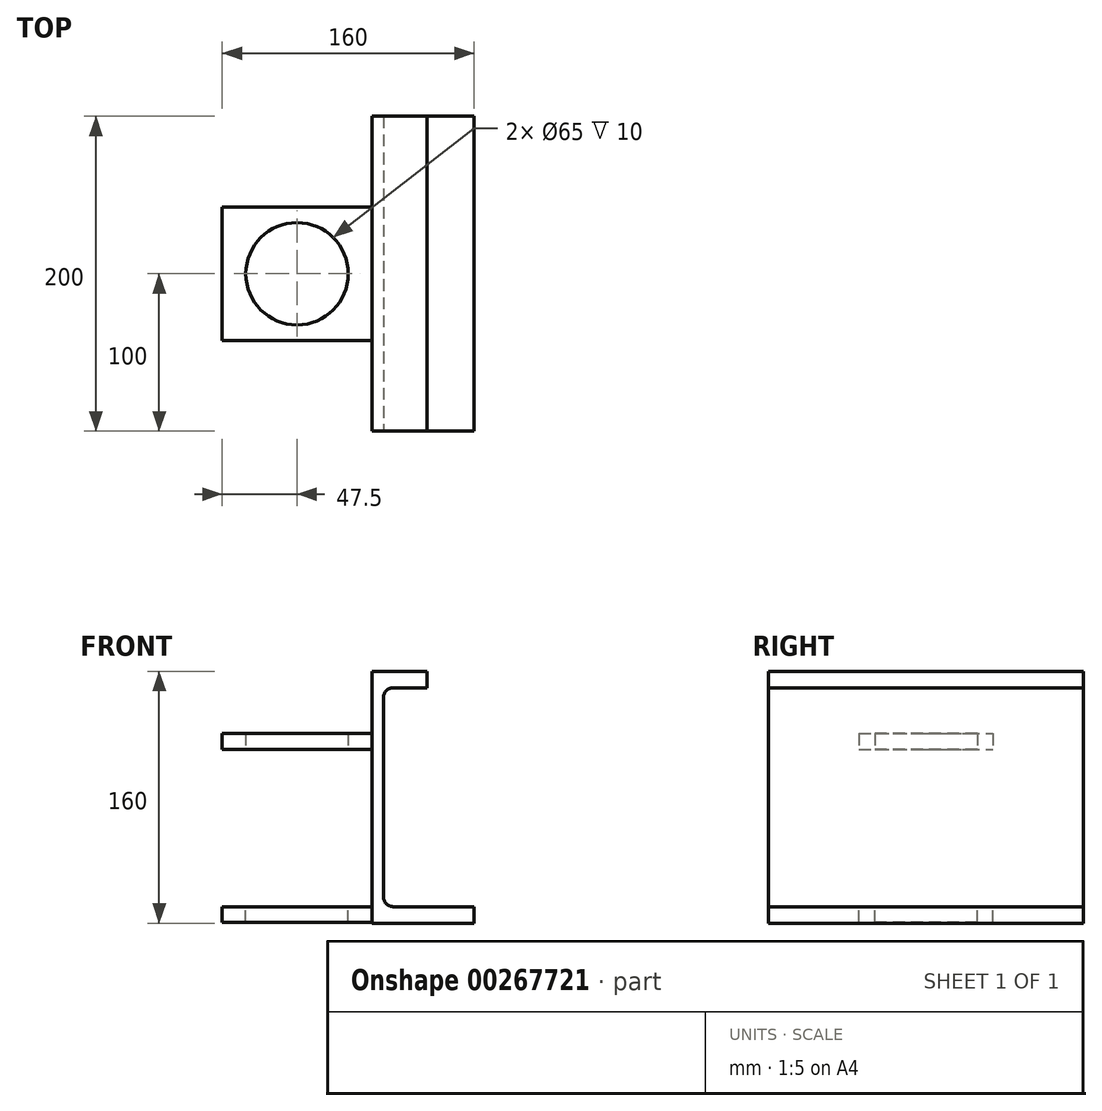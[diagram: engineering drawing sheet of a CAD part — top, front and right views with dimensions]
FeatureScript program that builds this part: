
annotation { "Feature Type Name" : "Feature", "Feature Type Description" : "" }
export const myFeature = defineFeature(function(context is Context, id is Id, definition is map)
    precondition{}
    {
        {
            var Q0;
            Q0=qCreatedBy(makeId("Front.planeOp"),FACE);
            var sketch = newSketch(context, id + "F0", { "sketchPlane" : qUnion([Q0])});
            skLineSegment(sketch, "E0.bottom", {"start": v(2.5, 80) * mm, "end": v(-32.5, 80) * mm});
            skLineSegment(sketch, "E0.top", {"start": v(32.5, -80) * mm, "end": v(-32.5, -80) * mm});
            skLineSegment(sketch, "E0.right", {"start": v(-32.5, 80) * mm, "end": v(-32.5, -80) * mm});
            skPoint(sketch, "E0.middle", {"position": v(0, 0) * mm});
            skLineSegment(sketch, "E1.0", {"start": v(2.5, 69.5) * mm, "end": v(-19, 69.5) * mm});
            skLineSegment(sketch, "E2.0", {"start": v(32.5, -69.5) * mm, "end": v(-19, -69.5) * mm});
            skLineSegment(sketch, "E3.0", {"start": v(-25, 63.5) * mm, "end": v(-25, -63.5) * mm});
            skArc(sketch, "E4.filletArc", {"start": v(-19, 69.5) * mm, "mid": v(-23.24, 67.74) * mm, "end": v(-25, 63.5) * mm});
            skArc(sketch, "E5.filletArc", {"start": v(-25, -63.5) * mm, "mid": v(-23.24, -67.74) * mm, "end": v(-19, -69.5) * mm});
            skLineSegment(sketch, "E6.trimOffspring", {"start": v(32.5, -69.5) * mm, "end": v(32.5, -80) * mm});
            skLineSegment(sketch, "E7", {"start": v(2.5, 80) * mm, "end": v(2.5, 69.5) * mm});
            skPoint(sketch, "E0.left.start.orphan", {"position": v(32.5, 80) * mm});
            skLineSegment(sketch, "E8.bottom", {"start": v(-32.5, 80) * mm, "end": v(-24.5, 80) * mm});
            skLineSegment(sketch, "E8.top", {"start": v(-32.5, 170) * mm, "end": v(-24.5, 170) * mm});
            skLineSegment(sketch, "E8.left", {"start": v(-32.5, 80) * mm, "end": v(-32.5, 170) * mm});
            skLineSegment(sketch, "E8.right", {"start": v(-24.5, 80) * mm, "end": v(-24.5, 170) * mm});
            skSolve(sketch);
        }
        {
            var Q0;
            {var subQ3=sQuery(id+"F0.wireOp",EDGE,"E0.bottom");Q0=makeQuery(id+"F0.imprint","IMPRINT",FACE,{"disambiguationData":[TD([[makeQuery(id+"F0.imprint","IMPRINT",EDGE,{"derivedFrom":subQ3}),1.0]])]});}
            var Q1;
            Q1=makeQuery(id+"F0.imprint","IMPRINT",FACE,{"disambiguationData":[TD([[makeQuery(id+"F0.imprint","IMPRINT",EDGE,{"derivedFrom":sQuery(id+"F0.wireOp",EDGE,"E8.bottom")}),1.0]])]});
            extrude(context, id + "F1", {"entities" : qUnion([Q0, Q1]), "oppositeDirection" : true, "depth" : 200 * mm});
        }
        {
            var Q0;
            Q0=makeQuery(id+"F1.opExtrude","SWEPT_FACE",FACE,{"disambiguationData":[OSD([sQuery(id+"F0.wireOp",EDGE,"E2.0")])]});
            cPlane(context, id + "F2", {"entities" : qUnion([Q0]), "cplaneType" : CPlaneType.OFFSET, "offset" : 0 * mm, "width" : 150 * mm, "height" : 150 * mm});
        }
        {
            var Q0;
            Q0=qCreatedBy(id+"F2.planeOp",FACE);
            var sketch = newSketch(context, id + "F3", { "sketchPlane" : qUnion([Q0])});
            skCircle(sketch, "E9", {"center": v(-80, 100) * mm, "radius": 32.5 * mm});
            skLineSegment(sketch, "E10.bottom", {"start": v(-127.5, 57.5) * mm, "end": v(-32.5, 57.5) * mm});
            skLineSegment(sketch, "E10.top", {"start": v(-127.5, 142.5) * mm, "end": v(-32.5, 142.5) * mm});
            skLineSegment(sketch, "E10.left", {"start": v(-127.5, 57.5) * mm, "end": v(-127.5, 142.5) * mm});
            skLineSegment(sketch, "E10.right", {"start": v(-32.5, 57.5) * mm, "end": v(-32.5, 142.5) * mm});
            skSolve(sketch);
        }
        {
            var Q0;
            Q0=qSketchRegion(id+"F3",true);
            extrude(context, id + "F4", {"entities" : qUnion([Q0]), "operationType" : NewBodyOperationType.ADD, "oppositeDirection" : true, "depth" : 10 * mm});
        }
        {
            var Q0;
            Q0=makeQuery(id+"F4.opExtrude","CAP_FACE",FACE,{"disambiguationData":[OSD([sQuery(id+"F3.wireOp",EDGE,"E9"),sQuery(id+"F3.wireOp",EDGE,"E10.bottom"),sQuery(id+"F3.wireOp",EDGE,"E10.top"),sQuery(id+"F3.wireOp",EDGE,"E10.left"),sQuery(id+"F3.wireOp",EDGE,"E10.right")])],"isStart":true});
            cPlane(context, id + "F5", {"entities" : qUnion([Q0]), "cplaneType" : CPlaneType.OFFSET, "offset" : 100 * mm, "width" : 150 * mm, "height" : 150 * mm});
        }
        {
            var Q0;
            Q0=qCreatedBy(id+"F5.planeOp",FACE);
            var sketch = newSketch(context, id + "F6", { "sketchPlane" : qUnion([Q0])});
            skCircle(sketch, "E11", {"center": v(-80, 100) * mm, "radius": 32.5 * mm});
            skLineSegment(sketch, "E12.bottom", {"start": v(-127.5, 57.5) * mm, "end": v(-32.5, 57.5) * mm});
            skLineSegment(sketch, "E12.top", {"start": v(-127.5, 142.5) * mm, "end": v(-32.5, 142.5) * mm});
            skLineSegment(sketch, "E12.left", {"start": v(-127.5, 57.5) * mm, "end": v(-127.5, 142.5) * mm});
            skLineSegment(sketch, "E12.right", {"start": v(-32.5, 57.5) * mm, "end": v(-32.5, 142.5) * mm});
            skSolve(sketch);
        }
        {
            var Q0;
            Q0=makeQuery(id+"F6.imprint","IMPRINT",FACE,{"disambiguationData":[TD([[makeQuery(id+"F6.imprint","IMPRINT",EDGE,{"derivedFrom":sQuery(id+"F6.wireOp",EDGE,"E11")}),-1.0]])]});
            extrude(context, id + "F7", {"entities" : qUnion([Q0]), "operationType" : NewBodyOperationType.ADD, "depth" : 10 * mm});
        }
        {
            var Q0;
            Q0=makeQuery(id+"F7.opExtrude","CAP_FACE",FACE,{"disambiguationData":[OSD([sQuery(id+"F6.wireOp",EDGE,"E11"),sQuery(id+"F6.wireOp",EDGE,"E12.bottom"),sQuery(id+"F6.wireOp",EDGE,"E12.top"),sQuery(id+"F6.wireOp",EDGE,"E12.left"),sQuery(id+"F6.wireOp",EDGE,"E12.right")])],"isStart":false});
            cPlane(context, id + "F8", {"entities" : qUnion([Q0]), "cplaneType" : CPlaneType.OFFSET, "offset" : 40 * mm, "width" : 150 * mm, "height" : 150 * mm});
        }
    });
